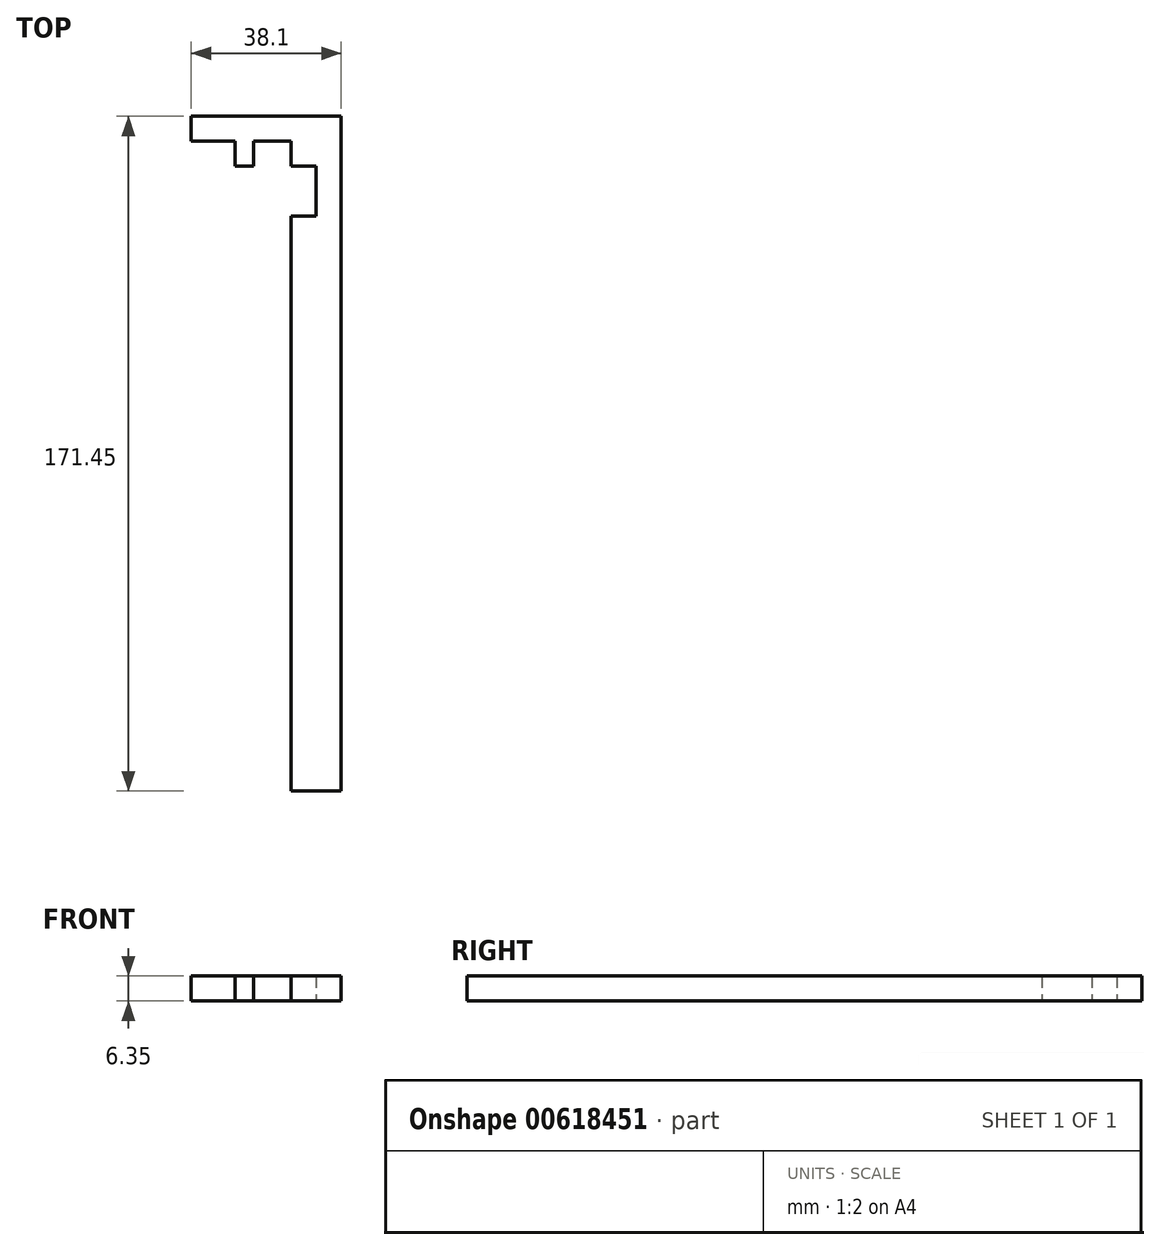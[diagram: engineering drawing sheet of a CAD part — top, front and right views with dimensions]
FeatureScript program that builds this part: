
annotation { "Feature Type Name" : "Feature", "Feature Type Description" : "" }
export const myFeature = defineFeature(function(context is Context, id is Id, definition is map)
    precondition{}
    {
        {
            var Q0;
            Q0=qCreatedBy(makeId("Top.planeOp"),FACE);
            var sketch = newSketch(context, id + "F0", { "sketchPlane" : qUnion([Q0])});
            skLineSegment(sketch, "E0.bottom", {"start": v(7.84, 15.69) * mm, "end": v(1.5, 15.69) * mm});
            skLineSegment(sketch, "E0.top", {"start": v(7.84, -136.71) * mm, "end": v(1.5, -136.71) * mm});
            skLineSegment(sketch, "E0.left", {"start": v(7.84, 15.69) * mm, "end": v(7.84, -136.71) * mm});
            skPoint(sketch, "E0.middle", {"position": v(1.5, -60.51) * mm});
            skLineSegment(sketch, "E1.top", {"start": v(7.84, 22.04) * mm, "end": v(1.5, 22.04) * mm});
            skLineSegment(sketch, "E1.left", {"start": v(7.84, 15.69) * mm, "end": v(7.84, 22.04) * mm});
            skLineSegment(sketch, "E1.right", {"start": v(1.5, 15.69) * mm, "end": v(1.5, 22.04) * mm});
            skLineSegment(sketch, "E2.bottom", {"start": v(7.84, 22.04) * mm, "end": v(-4.86, 22.04) * mm});
            skLineSegment(sketch, "E2.top", {"start": v(7.84, 28.39) * mm, "end": v(-4.86, 28.39) * mm});
            skLineSegment(sketch, "E2.left", {"start": v(7.84, 22.04) * mm, "end": v(7.84, 28.39) * mm});
            skLineSegment(sketch, "E2.right", {"start": v(-4.86, 22.04) * mm, "end": v(-4.86, 28.39) * mm});
            skLineSegment(sketch, "E3.bottom", {"start": v(7.84, 28.39) * mm, "end": v(-30.26, 28.39) * mm});
            skLineSegment(sketch, "E3.top", {"start": v(7.84, 34.74) * mm, "end": v(-30.26, 34.74) * mm});
            skLineSegment(sketch, "E3.left", {"start": v(7.84, 28.39) * mm, "end": v(7.84, 34.74) * mm});
            skLineSegment(sketch, "E3.right", {"start": v(-30.26, 28.39) * mm, "end": v(-30.26, 34.74) * mm});
            skLineSegment(sketch, "E4.bottom", {"start": v(-14.38, 28.39) * mm, "end": v(-19.14, 28.39) * mm});
            skLineSegment(sketch, "E4.top", {"start": v(-14.38, 22.04) * mm, "end": v(-19.14, 22.04) * mm});
            skLineSegment(sketch, "E4.left", {"start": v(-14.38, 28.39) * mm, "end": v(-14.38, 22.04) * mm});
            skLineSegment(sketch, "E4.right", {"start": v(-19.14, 28.39) * mm, "end": v(-19.14, 22.04) * mm});
            skLineSegment(sketch, "E5.left", {"start": v(1.5, 15.69) * mm, "end": v(1.5, -136.71) * mm});
            skLineSegment(sketch, "E6.bottom", {"start": v(1.5, -136.71) * mm, "end": v(-4.86, -136.71) * mm});
            skLineSegment(sketch, "E6.top", {"start": v(1.5, 9.34) * mm, "end": v(-4.86, 9.34) * mm});
            skLineSegment(sketch, "E6.left", {"start": v(1.5, -136.71) * mm, "end": v(1.5, 9.34) * mm});
            skLineSegment(sketch, "E6.right", {"start": v(-4.86, -136.71) * mm, "end": v(-4.86, 9.34) * mm});
            skSolve(sketch);
        }
        {
            var Q0;
            Q0=qSketchRegion(id+"F0",true);
            extrude(context, id + "F1", {"entities" : qUnion([Q0]), "depth" : 6.35 * mm, "offsetDistance" : 25.4 * mm});
        }
    });
